# Revit family: Mixer-Bath Shower-Dorf Epic1
name_source: partatom
category: Plumbing Fixtures
revit_build: Autodesk Revit Architecture 2012 (Build: 20110916_2132(x64)
units: mm (PartAtom-declared; Revit-internal decimal feet)

## types (1)
- Epic Bath/Shower Mixer
    Assembly Code = D2020300
    CW Connection = Yes
    CWFU = 2
    Connector Radius = 10 mm  [stored 0.0328084 ft]
    Cost = 0 $
    Default Elevation = 900 mm  [stored 2.95276 ft]
    Description = Fully featured cartridge, Chrome finish
    HW Connection = Yes
    HWFU = 2
    Height = 28 mm
    Manufacturer = Dorf
    Material_ANZRS = Metal-Chrome-Caroma
    Model = 6415.04
    Spout = 125 mm  [stored 0.410105 ft]
    Type Comments = Epic Bath/Shower Mixer
    URL = http://www.dorf.com.au
    Vent Connection = No
    Waste Connection = No

note: [stored X ft] marks values corroborated as IEEE doubles in the binary element streams (Revit-internal decimal feet)

## geometry (parser evidence)
native form markers: Blend x2, Sweep x2
no freeform markers — native parametric forms only
